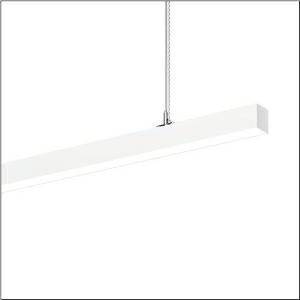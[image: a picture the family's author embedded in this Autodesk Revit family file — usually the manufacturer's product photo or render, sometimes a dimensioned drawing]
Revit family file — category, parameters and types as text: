
# Revit family: silica_r__21_51mx30tct9w_581c
name_source: partatom
category: Lighting Fixtures
units: mm (PartAtom-declared; Revit-internal decimal feet)

## family parameters
Cut with Voids When Loaded = No
Host = Face
Light Source = No
Part Type = Normal
Room Calculation Point = No
Round Connector Dimension = Use Diameter
Shared = No

## types (1)
- --- (1 x LED, 10300 lm, 84.4 W, 6500K)
    Apparent Load = 84 VA
    CIE Flux Codes = 47 79 96 58 100
    Color Rendering = 80
    Color Temperature = 6500K
    Default Elevation = 1800 mm
    Description = Silica® 21, office luminaire, primary optical cover: cover, of PMMA, opal, light emission: direct/indirect distribution, primary light characteristic: symmetric, installation type: suspended mounting, LED, rated luminous flux: 10.300lm, luminous efficacy: 116lm/W, light colour: 8tw, colour temperature: 2700..6500K, control gear: DALI DT8, with terminal, 3+2-pole, max. 2.5mm², mains connection: 220..240V, AC, 50/60Hz, rated input power: 88.7W, luminaire housing, of aluminium, traffic white (RAL 9016), length: 3.004mm, width: 53mm, height: 53mm, protection rating (complete): IP20, insulation class (complete): insulation class I (protective earthing), certification: CE, permissible operating ambient temperature: 0..+35°C, standard: EN 50419, packaging unit: 1 piece
    Height = 53 mm
    Lamp = 1 x LED
    Lamp Light Flux = 10300 lm
    Lamp Power = 84.4 W
    Lamp count = 1
    Length = 3004 mm
    Luminous efficacy = 122 lm/W
    Manufacturer = Siteco
    ModVariant = No
    Model = 51MX30TCT9W
    Mounting Place = Ceiling
    Mounting Type = Pendant
    Number of Poles = 1
    OnlyDefault = Yes
    Power Factor = 1
    Product Name = Silica® 21
    Product group = office luminaire | ceiling pendant
    ProductGroupID = 903
    Protection Class = Protection class I
    Protection Degree = IP 20
    RLX_Detail_Level = 1
    RLX_Emergency_Light_Flux = 0 lm
    RLX_Emergency_Type = 0
    RLX_Emergency_Type_DB = No
    RlxData = <blob elided: 17561 chars, md5=ad847a2a>
    Socket = socket
    Standby Power = 0 W
    System Light Flux = 10300 lm
    System Power = 84 W
    Type Comments = individual setting
    Type Image = l_1349023.jpg
    URL = http://relux.com
    VarID = @adj_161123
    Voltage = 0 V
    Weight = 0.00 kg
    Width = 53 mm

## geometry (parser evidence)
native form markers: Blend x4, Sweep x13
no freeform markers — native parametric forms only
